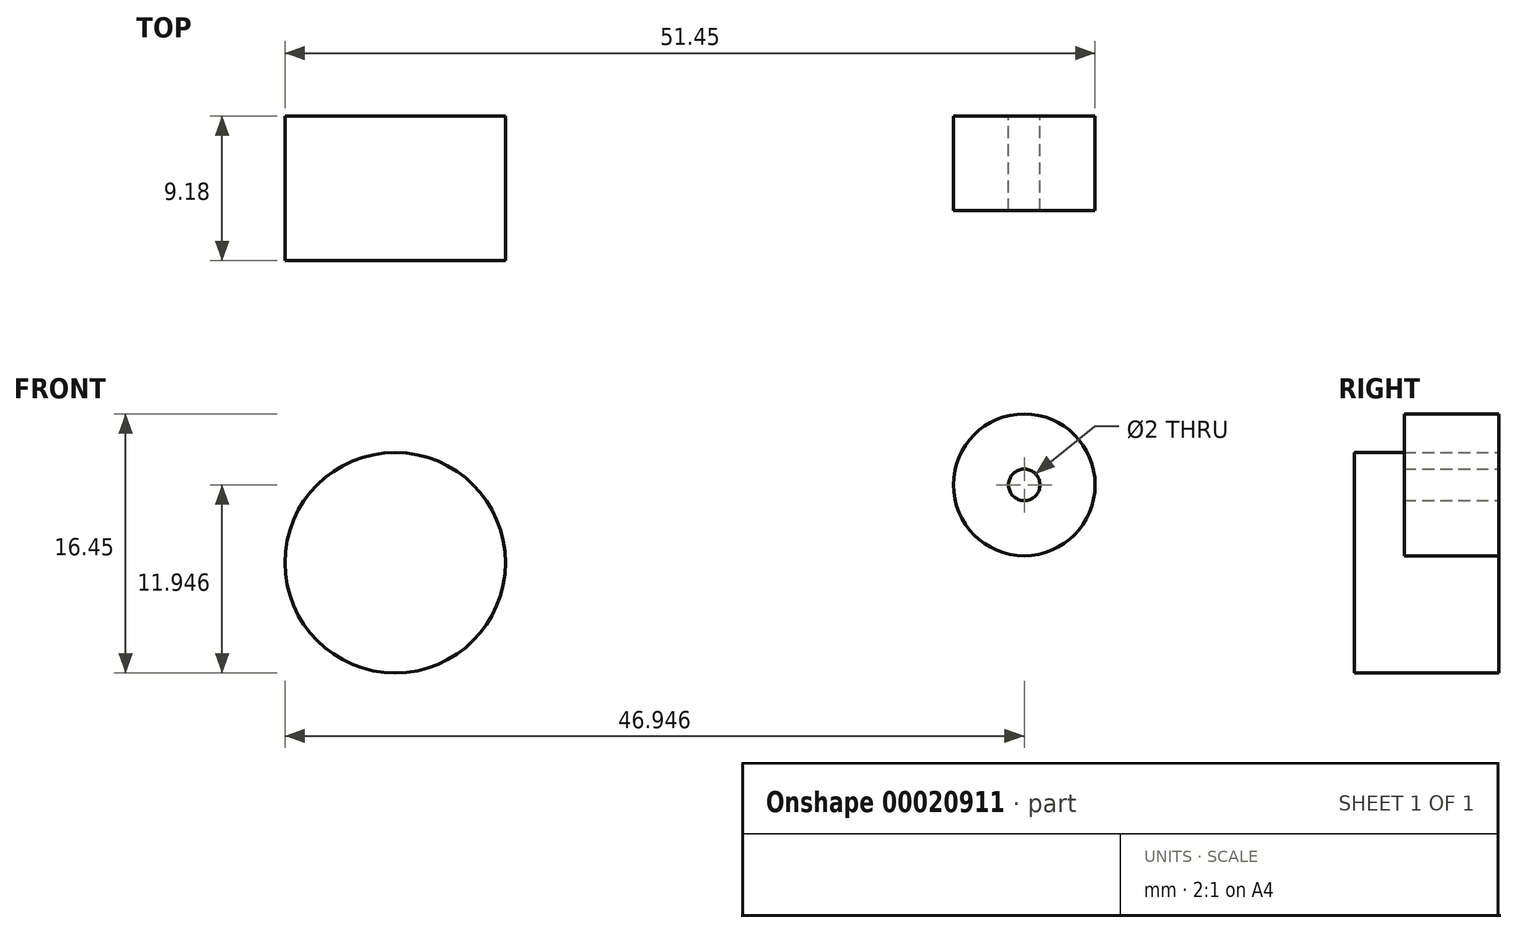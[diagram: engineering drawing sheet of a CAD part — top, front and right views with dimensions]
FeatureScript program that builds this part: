
annotation { "Feature Type Name" : "Feature", "Feature Type Description" : "" }
export const myFeature = defineFeature(function(context is Context, id is Id, definition is map)
    precondition{}
    {
        {
            var Q0;
            Q0=qCreatedBy(makeId("Front.planeOp"),FACE);
            var sketch = newSketch(context, id + "F0", { "sketchPlane" : qUnion([Q0])});
            skCircle(sketch, "E0", {"center": v(-75.2, 12.42) * mm, "radius": 7 * mm});
            skCircle(sketch, "E1", {"center": v(31.59, 18.92) * mm, "radius": 4.5 * mm});
            skCircle(sketch, "E2", {"center": v(31.59, 18.92) * mm, "radius": 1 * mm});
            skCircle(sketch, "E3", {"center": v(-75.2, 12.42) * mm, "radius": 3.5 * mm});
            skSolve(sketch);
        }
        {
            var Q0;
            Q0=qCreatedBy(makeId("Front.planeOp"),FACE);
            var sketch = newSketch(context, id + "F1", { "sketchPlane" : qUnion([Q0])});
            skCircle(sketch, "E4", {"center": v(-35.25, 17.37) * mm, "radius": 4.5 * mm});
            skCircle(sketch, "E5", {"center": v(-35.25, 17.37) * mm, "radius": 1 * mm});
            skSolve(sketch);
        }
        {
            var Q0;
            Q0=makeQuery(id+"F1.imprint","IMPRINT",FACE,{"disambiguationData":[TD([[makeQuery(id+"F1.imprint","IMPRINT",EDGE,{"derivedFrom":sQuery(id+"F1.wireOp",EDGE,"E4")}),1.0]])]});
            extrude(context, id + "F2", {"entities" : qUnion([Q0]), "depth" : 6 * mm});
        }
        {
            var Q0;
            Q0=makeQuery(id+"F0.imprint","IMPRINT",FACE,{"disambiguationData":[TD([[makeQuery(id+"F0.imprint","IMPRINT",EDGE,{"derivedFrom":sQuery(id+"F0.wireOp",EDGE,"E3")}),1.0]])]});
            var Q1;
            Q1=makeQuery(id+"F0.imprint","IMPRINT",FACE,{"disambiguationData":[TD([[makeQuery(id+"F0.imprint","IMPRINT",EDGE,{"derivedFrom":sQuery(id+"F0.wireOp",EDGE,"E0")}),1.0]])]});
            extrude(context, id + "F3", {"entities" : qUnion([Q0, Q1]), "depth" : 3.17 * mm});
        }
        {
            var Q0;
            Q0=makeQuery(id+"F3.opExtrude","CAP_FACE",FACE,{"disambiguationData":[OSD([sQuery(id+"F0.wireOp",EDGE,"E0")])],"isStart":false});
            var sketch = newSketch(context, id + "F4", { "sketchPlane" : qUnion([Q0])});
            skCircle(sketch, "E6", {"center": v(-75.2, 12.42) * mm, "radius": 3.5 * mm});
            skCircle(sketch, "E7", {"center": v(-75.2, 12.42) * mm, "radius": 2 * mm});
            skSolve(sketch);
        }
        {
            var Q0;
            Q0=makeQuery(id+"F4.imprint","IMPRINT",FACE,{"disambiguationData":[TD([[makeQuery(id+"F4.imprint","IMPRINT",EDGE,{"derivedFrom":sQuery(id+"F4.wireOp",EDGE,"E7")}),1.0]])]});
            extrude(context, id + "F5", {"entities" : qUnion([Q0]), "operationType" : NewBodyOperationType.ADD, "depth" : 6 * mm});
        }
        {
            var Q0;
            Q0=makeQuery(id+"F3.opExtrude","CAP_FACE",FACE,{"disambiguationData":[OSD([sQuery(id+"F0.wireOp",EDGE,"E0")])],"isStart":false});
            extrude(context, id + "F6", {"entities" : qUnion([Q0]), "operationType" : NewBodyOperationType.ADD, "depth" : 6 * mm});
        }
    });
